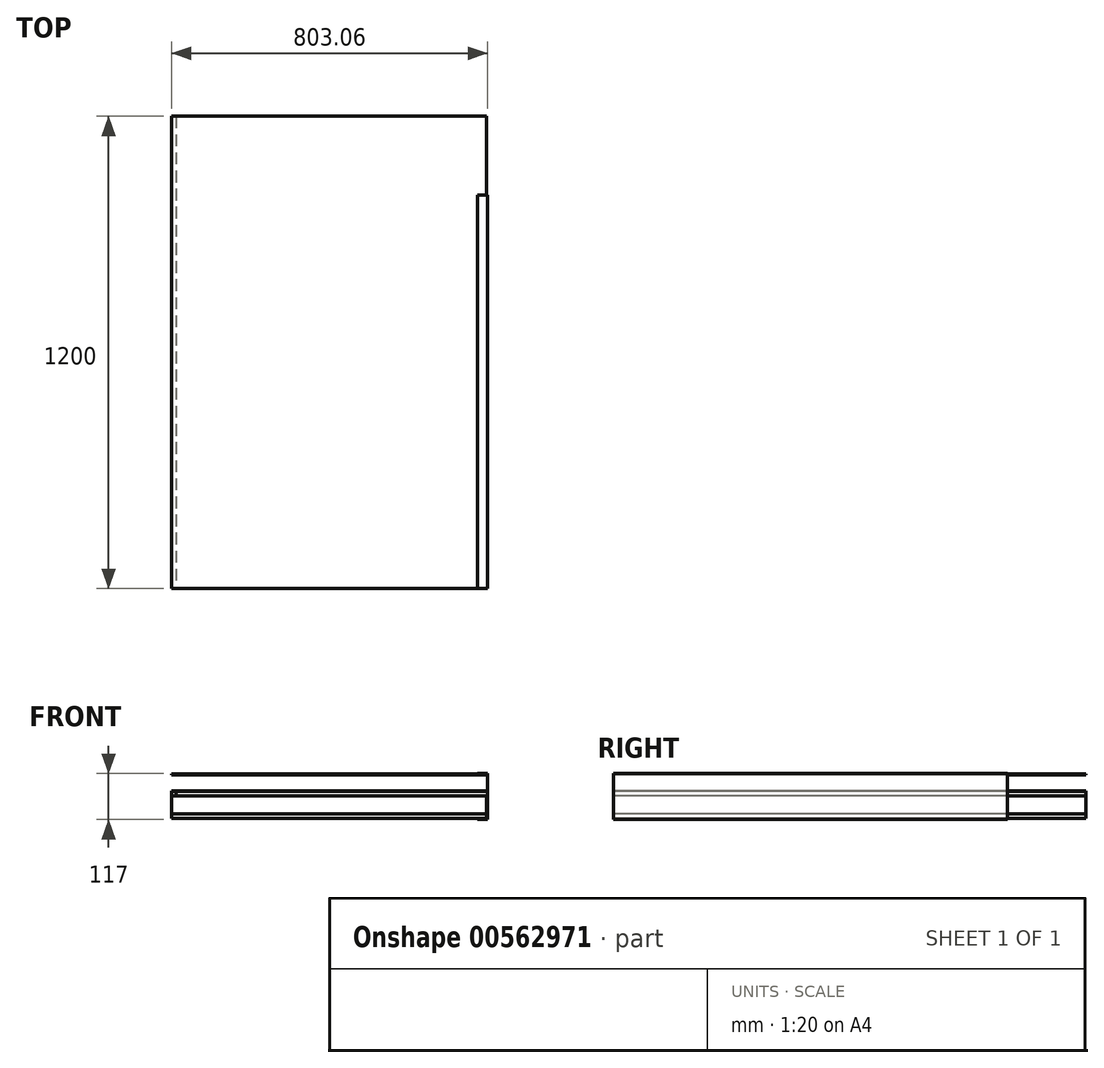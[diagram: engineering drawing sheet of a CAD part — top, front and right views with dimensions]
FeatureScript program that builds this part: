
annotation { "Feature Type Name" : "Feature", "Feature Type Description" : "" }
export const myFeature = defineFeature(function(context is Context, id is Id, definition is map)
    precondition{}
    {
        {
            var Q0;
            Q0=qCreatedBy(makeId("Top.planeOp"),FACE);
            var sketch = newSketch(context, id + "F0", { "sketchPlane" : qUnion([Q0])});
            skLineSegment(sketch, "E0.bottom", {"start": v(400, 600) * mm, "end": v(-400, 600) * mm});
            skLineSegment(sketch, "E0.top", {"start": v(400, -600) * mm, "end": v(-400, -600) * mm});
            skLineSegment(sketch, "E0.left", {"start": v(400, 600) * mm, "end": v(400, -600) * mm});
            skLineSegment(sketch, "E0.right", {"start": v(-400, 600) * mm, "end": v(-400, -600) * mm});
            skPoint(sketch, "E0.middle", {"position": v(0, 0) * mm});
            skSolve(sketch);
        }
        {
            var Q0;
            Q0 = qSketchRegion(id + "F0", true);
            extrude(context, id + "F1", {"entities" : qUnion([Q0]), "depth" : 12 * mm, "offsetDistance" : 25 * mm});
        }
        {
            var Q0;
            Q0=makeQuery(id+"F1.opExtrude","CAP_FACE",FACE,{"disambiguationData":[OSD([sQuery(id+"F0.wireOp",EDGE,"E0.bottom"),sQuery(id+"F0.wireOp",EDGE,"E0.top"),sQuery(id+"F0.wireOp",EDGE,"E0.left"),sQuery(id+"F0.wireOp",EDGE,"E0.right")])],"isStart":false});
            extrude(context, id + "F2", {"entities" : qUnion([Q0]), "depth" : 45 * mm, "offsetDistance" : 25 * mm});
        }
        {
            var Q0;
            Q0=makeQuery(id+"F2.opExtrude","SWEPT_FACE",FACE,{"disambiguationData":[OSD([sQuery(id+"F0.wireOp",EDGE,"E0.top")])]});
            var sketch = newSketch(context, id + "F3", { "sketchPlane" : qUnion([Q0])});
            skLineSegment(sketch, "E1.bottom", {"start": v(-400, 57) * mm, "end": v(-388, 57) * mm});
            skLineSegment(sketch, "E1.top", {"start": v(-400, 69) * mm, "end": v(-388, 69) * mm});
            skLineSegment(sketch, "E1.left", {"start": v(-400, 57) * mm, "end": v(-400, 69) * mm});
            skLineSegment(sketch, "E1.right", {"start": v(-388, 57) * mm, "end": v(-388, 69) * mm});
            skSolve(sketch);
        }
        {
            var Q0;
            Q0 = qSketchRegion(id + "F3", true);
            var Q1;
            Q1=makeQuery(id+"F2.opExtrude","SWEPT_FACE",FACE,{"disambiguationData":[OSD([sQuery(id+"F0.wireOp",EDGE,"E0.bottom")])]});
            extrude(context, id + "F4", {"entities" : qUnion([Q0]), "endBound" : BoundingType.UP_TO_SURFACE, "oppositeDirection" : true, "depth" : 25 * mm, "endBoundEntityFace" : qUnion([Q1]), "offsetDistance" : 25 * mm});
        }
        {
            var Q0;
            Q0=makeQuery(id+"F4.opExtrude","SWEPT_FACE",FACE,{"disambiguationData":[OSD([sQuery(id+"F3.wireOp",EDGE,"E1.top")])]});
            var sketch = newSketch(context, id + "F5", { "sketchPlane" : qUnion([Q0])});
            skLineSegment(sketch, "E2.bottom", {"start": v(400, 600) * mm, "end": v(-400, 600) * mm});
            skLineSegment(sketch, "E2.top", {"start": v(400, -600) * mm, "end": v(-400, -600) * mm});
            skLineSegment(sketch, "E2.left", {"start": v(400, 600) * mm, "end": v(400, -600) * mm});
            skLineSegment(sketch, "E2.right", {"start": v(-400, 600) * mm, "end": v(-400, -600) * mm});
            skPoint(sketch, "E2.middle", {"position": v(0, 0) * mm});
            skSolve(sketch);
        }
        {
            var Q0;
            Q0 = qSketchRegion(id + "F5", true);
            extrude(context, id + "F6", {"entities" : qUnion([Q0]), "depth" : 0.6 * mm, "offsetDistance" : 25 * mm});
        }
        {
            var Q0;
            Q0=makeQuery(id+"F2.opExtrude","SWEPT_FACE",FACE,{"disambiguationData":[OSD([sQuery(id+"F0.wireOp",EDGE,"E0.top")])]});
            var sketch = newSketch(context, id + "F7", { "sketchPlane" : qUnion([Q0])});
            skLineSegment(sketch, "E3", {"start": v(377.06, 113.17) * mm, "end": v(402.06, 113.17) * mm});
            skLineSegment(sketch, "E4", {"start": v(402.06, 113.17) * mm, "end": v(402.06, -1.83) * mm});
            skLineSegment(sketch, "E5", {"start": v(402.06, -1.83) * mm, "end": v(377.06, -1.83) * mm});
            skLineSegment(sketch, "E6", {"start": v(377.06, -1.83) * mm, "end": v(377.06, -2.83) * mm});
            skLineSegment(sketch, "E7", {"start": v(377.06, -2.83) * mm, "end": v(403.06, -2.83) * mm});
            skLineSegment(sketch, "E8", {"start": v(403.06, -2.83) * mm, "end": v(403.06, 114.17) * mm});
            skLineSegment(sketch, "E9", {"start": v(403.06, 114.17) * mm, "end": v(377.06, 114.17) * mm});
            skLineSegment(sketch, "E10", {"start": v(377.06, 114.17) * mm, "end": v(377.06, 113.17) * mm});
            skLineSegment(sketch, "E11", {"start": v(402.06, 113.17) * mm, "end": v(402.06, 114.17) * mm, "construction": true});
            skLineSegment(sketch, "E12", {"start": v(402.06, 113.17) * mm, "end": v(403.06, 113.17) * mm, "construction": true});
            skSolve(sketch);
        }
        {
            var Q0;
            Q0 = qSketchRegion(id + "F7", true);
            extrude(context, id + "F8", {"entities" : qUnion([Q0]), "oppositeDirection" : true, "depth" : 1000 * mm, "offsetDistance" : 25 * mm});
        }
        {
            var Q0;
            Q0=makeQuery(id+"F8.opExtrude","SWEPT_FACE",FACE,{"disambiguationData":[OSD([sQuery(id+"F7.wireOp",EDGE,"E3")])]});
            var sketch = newSketch(context, id + "F9", { "sketchPlane" : qUnion([Q0])});
            skLineSegment(sketch, "E13.bottom", {"start": v(-400, -600) * mm, "end": v(400, -600) * mm});
            skLineSegment(sketch, "E13.top", {"start": v(-400, 600) * mm, "end": v(400, 600) * mm});
            skLineSegment(sketch, "E13.left", {"start": v(-400, -600) * mm, "end": v(-400, 600) * mm});
            skLineSegment(sketch, "E13.right", {"start": v(400, -600) * mm, "end": v(400, 600) * mm});
            skPoint(sketch, "E13.middle", {"position": v(0, 0) * mm});
            skSolve(sketch);
        }
        {
            var Q0;
            Q0 = qSketchRegion(id + "F9", true);
            extrude(context, id + "F10", {"entities" : qUnion([Q0]), "depth" : 2 * mm, "offsetDistance" : 25 * mm});
        }
    });
